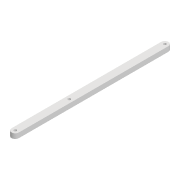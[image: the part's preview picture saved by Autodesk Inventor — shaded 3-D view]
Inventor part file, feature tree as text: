
AUTODESK INVENTOR PART (.ipt)
format: ipt  version: 2022 (Build 260153000, 153)  size: 90,112 bytes
history: native  units: mm
features: extrude x1, sketch x1
ambient origin geometry x8: Origin, YZ Plane, XZ Plane, XY Plane, X Axis, Y Axis, Z Axis, Center Point
bodies: Solid1 (feature_tree)
feature tree (2):
  extrude  "Extrusion1"  Depth=4.0mm
  sketch  "Sketch1"  dims[d0=2.2mm d1=2.2mm d2=6.0mm d3=122.139mm d4=2.2mm d5=44.122mm d6=4.0mm d7=0.0mm]
